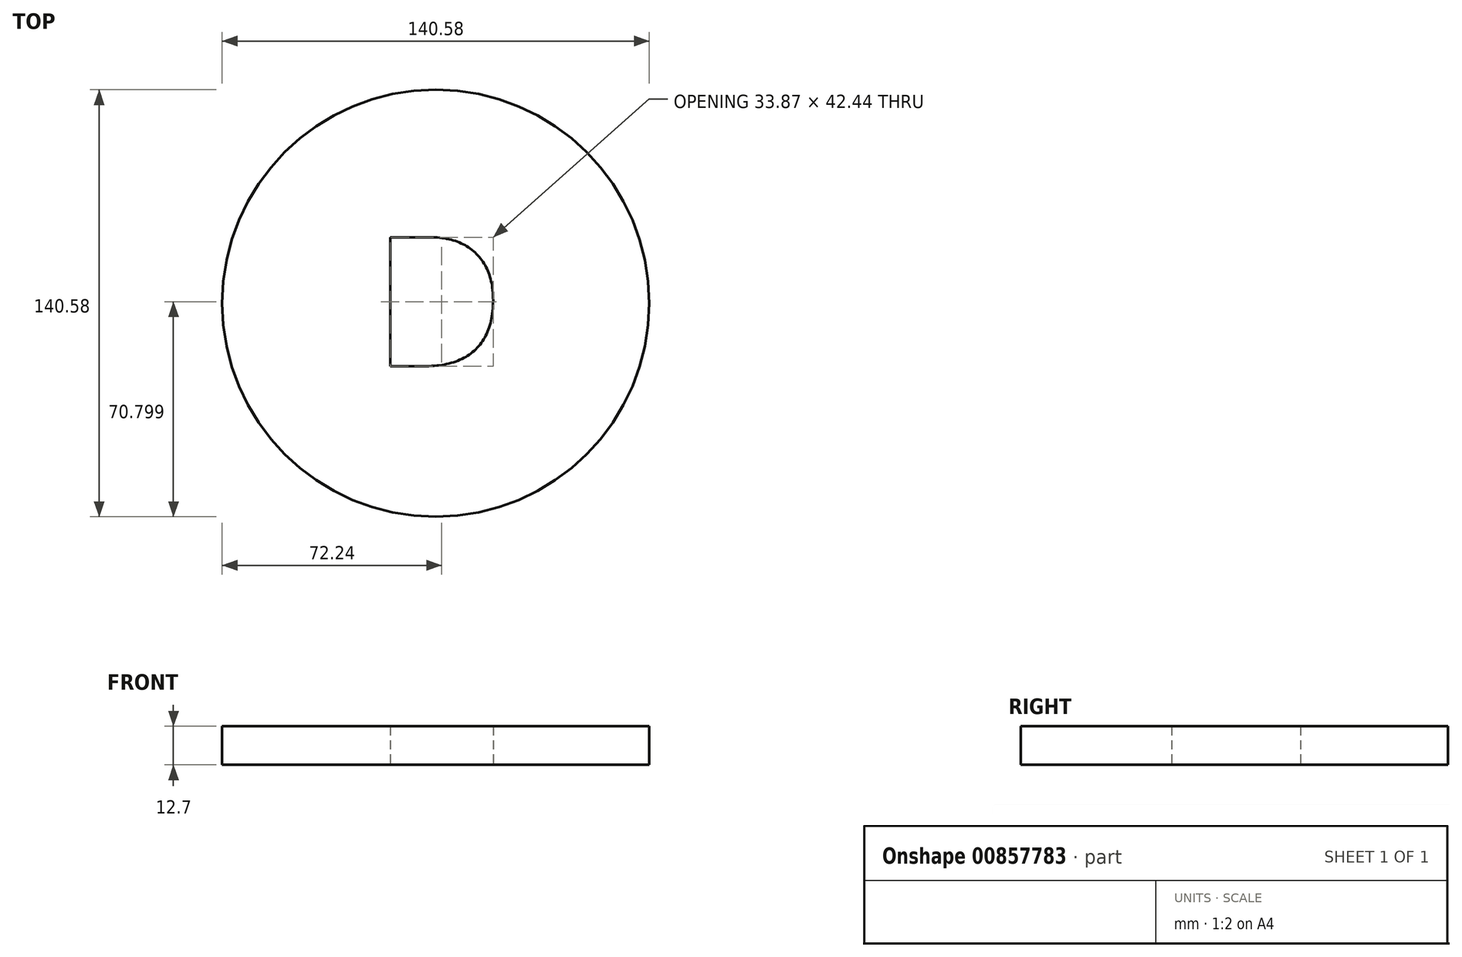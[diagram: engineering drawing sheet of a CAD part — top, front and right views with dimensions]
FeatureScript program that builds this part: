
annotation { "Feature Type Name" : "Feature", "Feature Type Description" : "" }
export const myFeature = defineFeature(function(context is Context, id is Id, definition is map)
    precondition{}
    {
        {
            var Q0;
            Q0=qCreatedBy(makeId("Top.planeOp"),FACE);
            var sketch = newSketch(context, id + "F0", { "sketchPlane" : qUnion([Q0])});
            skCircle(sketch, "E0", {"center": v(0, 0) * mm, "radius": 70.29 * mm});
            skText(sketch, "E1", { "text": "D", "fontName": "OpenSans-Regular.ttf"});
            const initialGuessF0  = {"E1": [-0.02082, -0.02071, 1, 0, 0.0428]};
            skSetInitialGuess(sketch, initialGuessF0);
            skSolve(sketch);
        }
        {
            var Q0;
            Q0=makeQuery(id+"F0.imprint","IMPRINT",FACE,{"disambiguationData":[TD([[makeQuery(id+"F0.imprint","IMPRINT",EDGE,{"derivedFrom":sQuery(id+"F0.wireOp",EDGE,"E0")}),1.0]])]});
            extrude(context, id + "F1", {"entities" : qUnion([Q0]), "depth" : 12.7 * mm, "offsetDistance" : 25.4 * mm});
        }
    });
